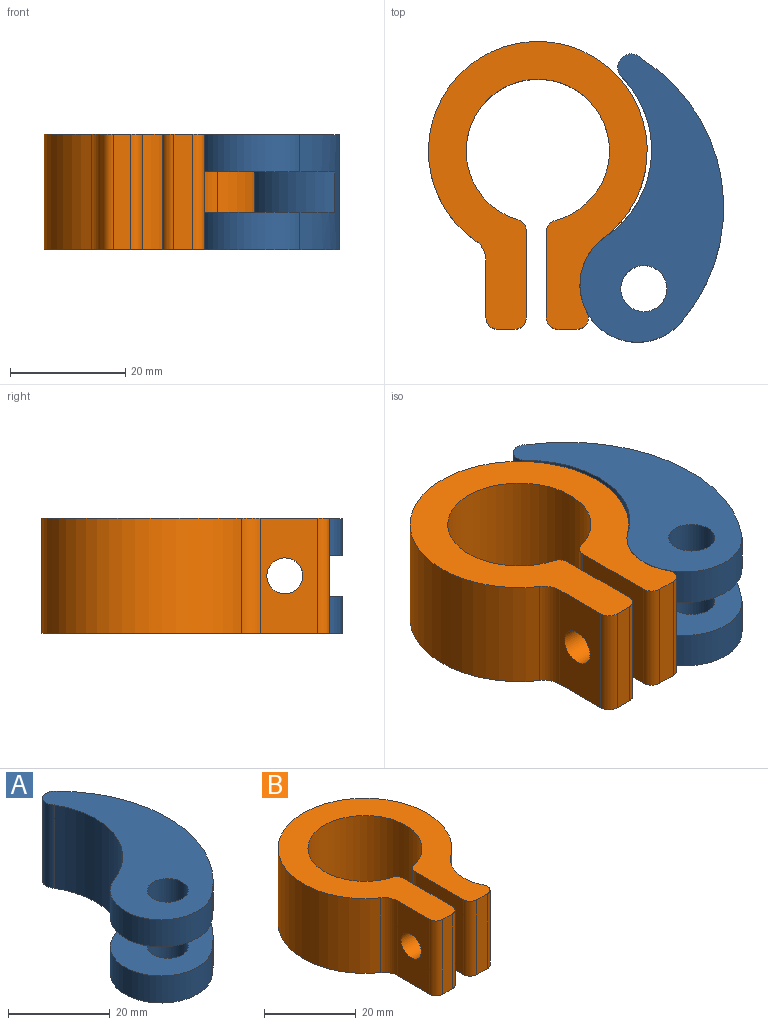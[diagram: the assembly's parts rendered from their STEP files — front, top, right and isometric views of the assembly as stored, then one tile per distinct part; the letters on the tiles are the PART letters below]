
ASSEMBLY  parts=2 mates=1
PART A: 12 faces, bbox 28.4x49.4x20 mm
  f0: cylinder r=18.19mm len=26.14mm, axis (0,0,-1), area 572.4mm2, adj f1,f4,f5,f6,f7,f9,f10,f11
  f1: cylinder r=10mm len=19.22mm, axis (0,0,-1), area 224.7mm2, adj f0,f2,f7,f10
  f2: cylinder r=30.54mm len=45.64mm, axis (0,0,-1), area 938mm2, adj f1,f4,f5,f6,f7,f9,f10,f11
  f3: cylinder r=4mm len=8mm, axis (0,0,1), area 163.4mm2, adj f7,f10
  f4: cylinder r=10mm len=19.22mm, axis (0,0,-1), area 224.7mm2, adj f0,f2,f6,f11
  f5: cylinder r=2.38mm len=20mm, axis (0,0,-1), area 162.3mm2, adj f0,f2,f6,f7
  f6: plane 49.36x28.4mm, normal (0,0,1), area 649.9mm2, adj f0,f2,f4,f5,f8
  f7: plane 49.36x28.4mm, normal (0,0,-1), area 649.9mm2, adj f0,f1,f2,f3,f5
  f8: cylinder r=4mm len=8mm, axis (0,0,1), area 163.4mm2, adj f6,f11
  f9: cylinder r=14.92mm len=11.8mm, axis (0,0,1), area 120mm2, adj f0,f2,f10,f11
  f10: plane 25.18x24.07mm, normal (0,0,1), area 311.7mm2, adj f0,f1,f2,f3,f9
  f11: plane 25.18x24.07mm, normal (0,0,-1), area 311.7mm2, adj f0,f2,f4,f8,f9
PART B: 19 faces, bbox 38x50x20 mm
  f0: cylinder r=10mm len=20mm, axis (0,0,-1), area 246.4mm2, adj f1,f14,f15,f16,f17
  f1: cylinder r=19mm len=38mm, axis (0,0,-1), area 1924.7mm2, adj f0,f2,f15,f16
  f2: cylinder r=4mm len=20mm, axis (0,0,-1), area 77.6mm2, adj f1,f3,f15,f16
  f3: plane 20x10.03mm, normal (-1,0,0), area 169.9mm2, adj f2,f4,f15,f16,f18
  f4: cylinder r=2mm len=20mm, axis (0,0,-1), area 62.8mm2, adj f3,f5,f15,f16
  f5: plane 20x3mm, normal (0,-1,0), area 60mm2, adj f4,f6,f15,f16
  f6: cylinder r=2mm len=20mm, axis (0,0,-1), area 62.8mm2, adj f5,f7,f15,f16
  f7: plane 20x15.11mm, normal (1,0,0), area 271.6mm2, adj f6,f8,f15,f16,f18
  f8: cylinder r=2mm len=20mm, axis (0,0,-1), area 51.6mm2, adj f7,f9,f15,f16
  f9: cylinder r=12.45mm len=24.9mm, axis (0,0,-1), area 1433.8mm2, adj f8,f10,f15,f16
  f10: cylinder r=2mm len=20mm, axis (0,0,-1), area 53mm2, adj f9,f11,f15,f16
  f11: plane 20x14.98mm, normal (-1,0,0), area 268.9mm2, adj f10,f12,f15,f16,f17
  f12: cylinder r=2mm len=20mm, axis (0,0,-1), area 62.8mm2, adj f11,f13,f15,f16
  f13: plane 20x3.28mm, normal (0,-1,0), area 65.7mm2, adj f12,f14,f15,f16
  f14: cylinder r=2mm len=20mm, axis (0,0,-1), area 82.8mm2, adj f0,f13,f15,f16
  f15: plane 50x38mm, normal (0,0,1), area 795.1mm2, adj f0,f1,f2,f3,f4,f5,f6,f7
  f16: plane 50x38mm, normal (0,0,-1), area 795.1mm2, adj f0,f1,f2,f3,f4,f5,f6,f7
  f17: cylinder r=3.12mm len=6.32mm, axis (-1,0,0), area 119mm2, adj f0,f11
  f18: cylinder r=3.12mm len=7mm, axis (-1,0,0), area 137.4mm2, adj f3,f7
PLACE A rot(axis=(0,0,1),13deg) t=(0.55,-24.72,-6.74)mm
PLACE B t=(-16.76,-1.47,-6.69)mm fixed
MATE revolute B.f0 <-> A.f1  axis (0,0,-1) through (0.55,-24.72,13.31)mm
